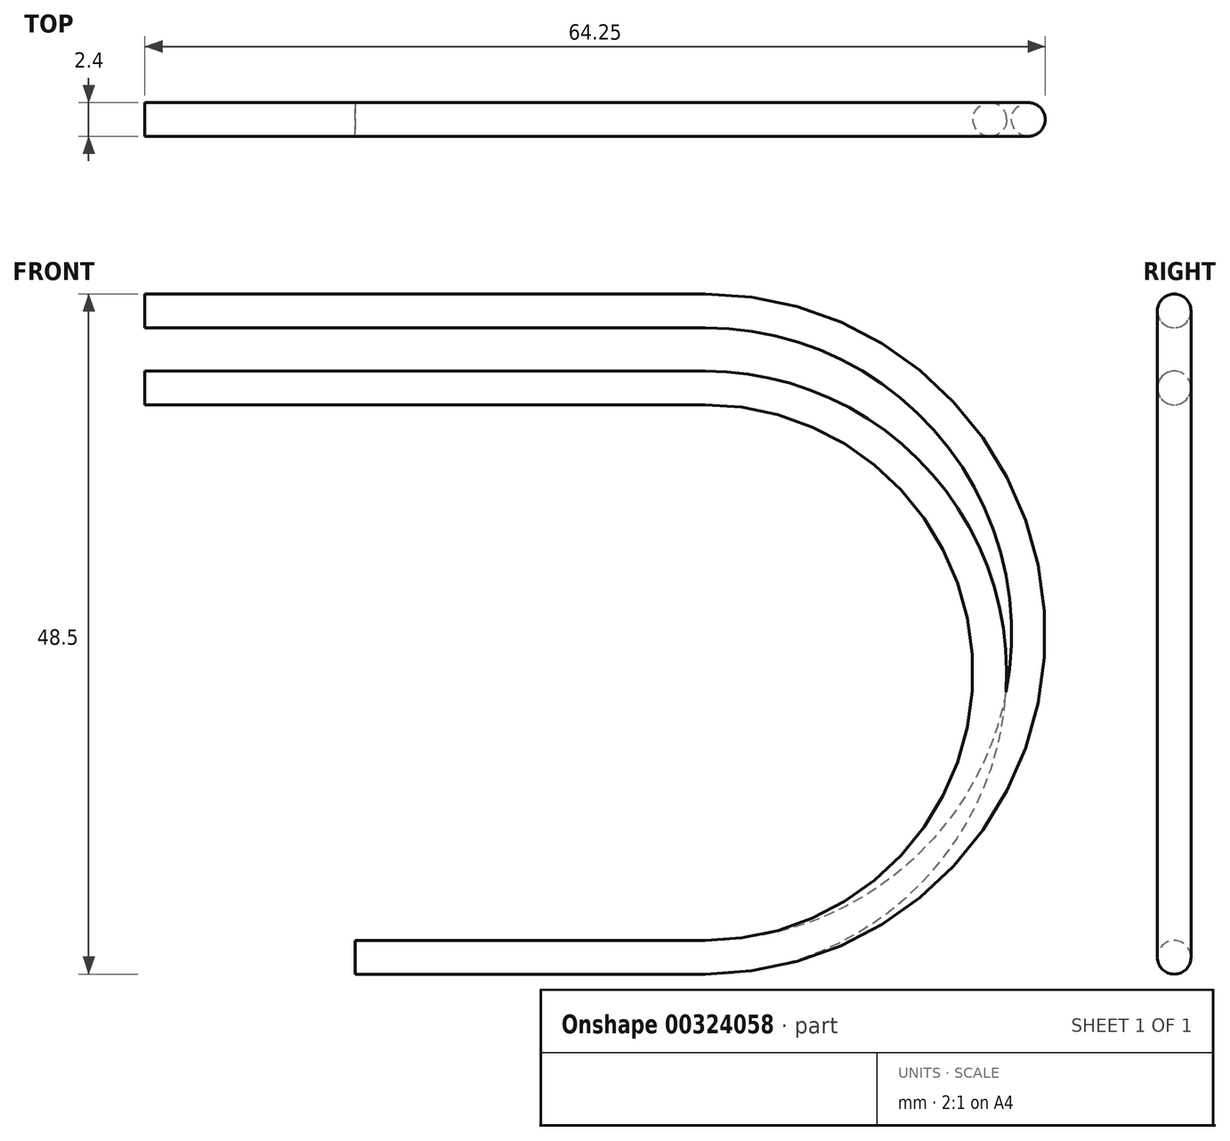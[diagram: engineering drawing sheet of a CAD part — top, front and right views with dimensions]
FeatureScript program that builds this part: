
annotation { "Feature Type Name" : "Feature", "Feature Type Description" : "" }
export const myFeature = defineFeature(function(context is Context, id is Id, definition is map)
    precondition{}
    {
        {
            var Q0;
            Q0=qCreatedBy(makeId("Front.planeOp"),FACE);
            var sketch = newSketch(context, id + "F0", { "sketchPlane" : qUnion([Q0])});
            skLineSegment(sketch, "E0", {"start": v(0, 0) * mm, "end": v(25, 0) * mm});
            skLineSegment(sketch, "E1", {"start": v(25, 0) * mm, "end": v(25, 40.6) * mm, "construction": true});
            skLineSegment(sketch, "E2", {"start": v(25, 40.6) * mm, "end": v(-15, 40.6) * mm});
            skArc(sketch, "E3", {"start": v(25, 0) * mm, "mid": v(45.3, 20.3) * mm, "end": v(25, 40.6) * mm});
            skLineSegment(sketch, "E4", {"start": v(25, 0) * mm, "end": v(25, 46.1) * mm, "construction": true});
            skLineSegment(sketch, "E5", {"start": v(25, 46.1) * mm, "end": v(-15, 46.1) * mm});
            skArc(sketch, "E6", {"start": v(25, 0) * mm, "mid": v(48.05, 23.05) * mm, "end": v(25, 46.1) * mm});
            skSolve(sketch);
        }
        {
            var Q0;
            Q0=qCreatedBy(makeId("Right.planeOp"),FACE);
            var sketch = newSketch(context, id + "F1", { "sketchPlane" : qUnion([Q0])});
            skCircle(sketch, "E7", {"center": v(0, 0) * mm, "radius": 1.2 * mm});
            skSolve(sketch);
        }
        {
            var Q0;
            Q0=makeQuery(id+"F1.imprint","IMPRINT",FACE,{"disambiguationData":[TD([[makeQuery(id+"F1.imprint","IMPRINT",EDGE,{"derivedFrom":sQuery(id+"F1.wireOp",EDGE,"E7")}),1.0]])]});
            var Q1;
            Q1=sQuery(id+"F1.wireOp",EDGE,"E7");
            var Q2;
            Q2=sQuery(id+"F0.wireOp",EDGE,"E0");
            var Q3;
            Q3=sQuery(id+"F0.wireOp",EDGE,"E3");
            var Q4;
            Q4=sQuery(id+"F0.wireOp",EDGE,"E2");
            sweep(context, id + "F2", {"profiles" : qUnion([Q0]), "surfaceProfiles" : qUnion([Q1]), "path" : qUnion([Q2, Q3, Q4])});
        }
        {
            var Q0;
            Q0=makeQuery(id+"F1.imprint","IMPRINT",FACE,{"disambiguationData":[TD([[makeQuery(id+"F1.imprint","IMPRINT",EDGE,{"derivedFrom":sQuery(id+"F1.wireOp",EDGE,"E7")}),1.0]])]});
            var Q1;
            Q1=sQuery(id+"F0.wireOp",EDGE,"E0");
            var Q2;
            Q2=sQuery(id+"F0.wireOp",EDGE,"E6");
            var Q3;
            Q3=sQuery(id+"F0.wireOp",EDGE,"E5");
            sweep(context, id + "F3", {"profiles" : qUnion([Q0]), "path" : qUnion([Q1, Q2, Q3])});
        }
    });
